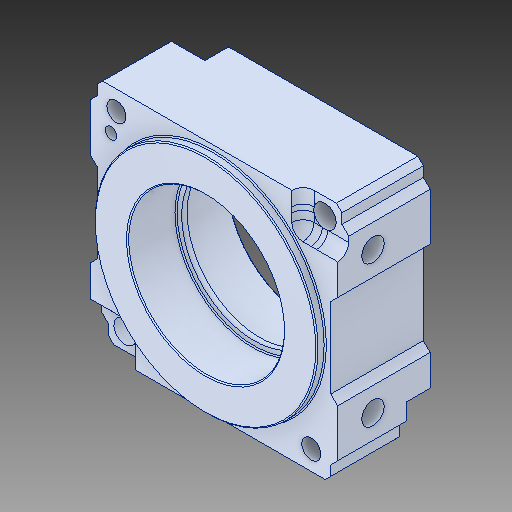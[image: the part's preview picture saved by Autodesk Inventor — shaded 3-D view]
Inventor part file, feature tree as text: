
AUTODESK INVENTOR PART (.ipt)
format: ipt  version: 2018 (Build 220112000, 112)  size: 259,584 bytes
history: native  units: in
note: dims shown in document units (in); Inventor stores cm internally (conversion verified against a paired STEP export)
features: chamfer x1
ambient origin geometry x8: Origin, YZ Plane, XZ Plane, XY Plane, X Axis, Y Axis, Z Axis, Center Point
bodies: Solid1 (feature_tree)
feature tree (1):
  chamfer  "Chamfer2"  [1 undecoded]
note: 1 required parameter value undecoded (feature->parameter linkage not recoverable at this tier; creation-order binding heuristic only, values carry confidence <= 0.55)
